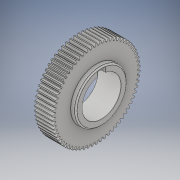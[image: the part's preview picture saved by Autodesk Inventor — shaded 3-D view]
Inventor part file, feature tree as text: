
AUTODESK INVENTOR PART (.ipt)
format: ipt  version: 2018 (Build 220112000, 112)  size: 1,092,608 bytes
history: native  units: mm
features: extrude x3, sketch x3, fillet x2, chamfer x1
ambient origin geometry x8: Origin, YZ Plane, XZ Plane, XY Plane, X Axis, Y Axis, Z Axis, Center Point
bodies: Solid1 (feature_tree)
feature tree (9):
  extrude  "Extrusion1"  Depth=31.76mm
  extrude  "Extrusion2"  Depth=0.57mm
  chamfer  "Chamfer1"  Distance=0.2mm
  fillet  "Fillet1"  Radius=6.39mm
  extrude  "Extrusion3"  Depth=0.1mm TaperAngle=360.0deg
  fillet  "Fillet2"  Radius=7.0mm
  sketch  "Sketch1"  dims[d0=15.0mm d1=31.76mm d2=34.0mm]
  sketch  "Sketch2"  dims[d3=0.135mm d4=0.57mm]
  sketch  "Sketch3"  dims[d5=0.2mm d6=0.2mm d7=6.39mm d8=660.0mm d10=360.0deg d12=7.0mm d13=0.0mm d14=20.0mm d15=2.0mm d16=0.0mm d17=0.5mm d18=2.0mm d19=45.0deg d20=0.1mm d21=9.0mm d22=3.0mm d23=20.5mm d24=0.0mm d25=0.1mm]
